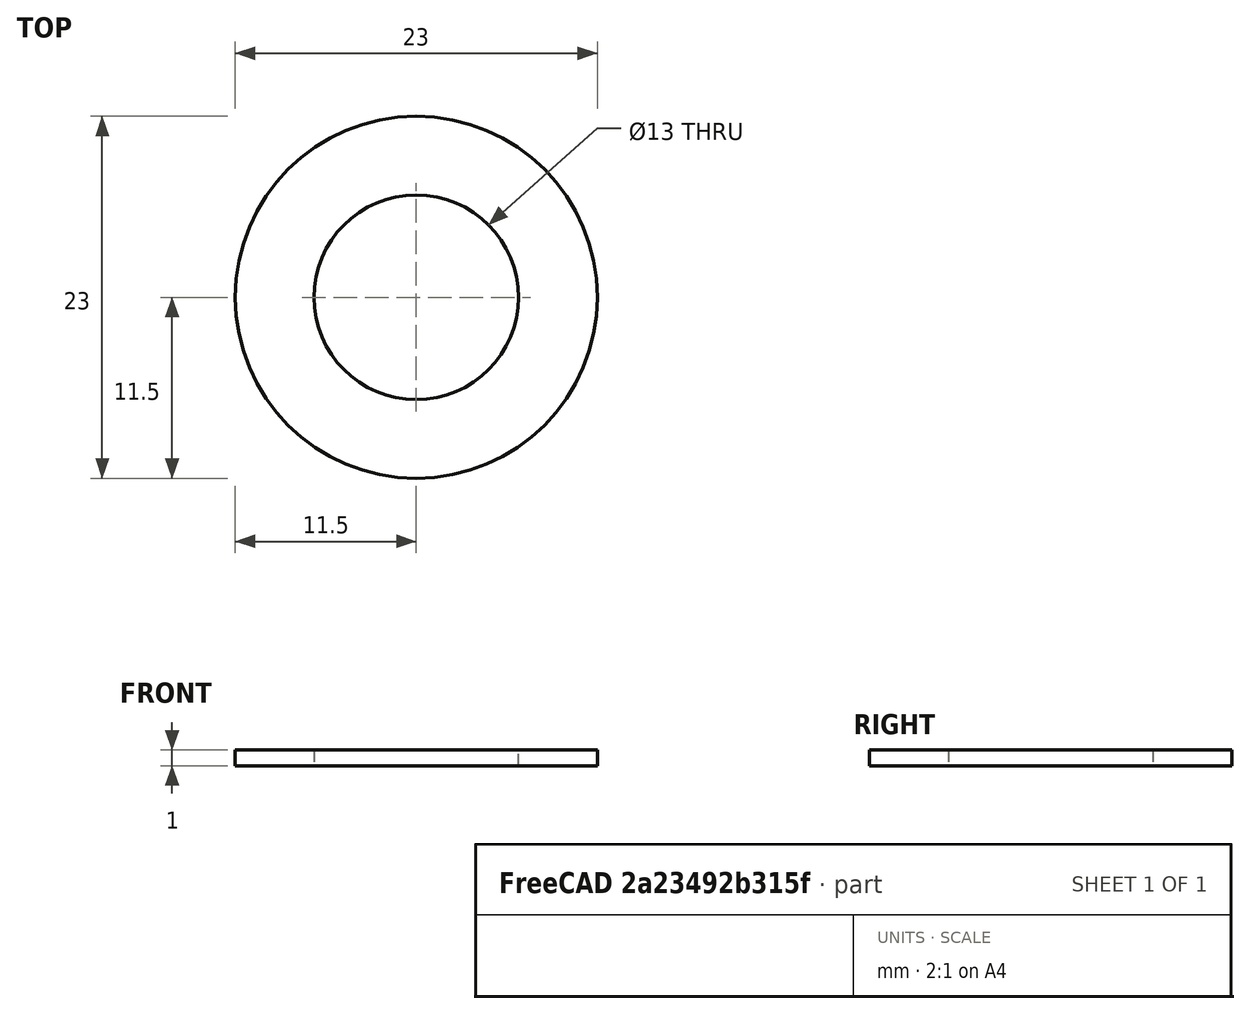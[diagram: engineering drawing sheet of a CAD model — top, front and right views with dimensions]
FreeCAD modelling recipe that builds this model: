
FCSTD DOCUMENT  (FreeCAD 0.19R24276 (Git))
Label: Ring_d13_d23_h1_v2
License: All rights reserved
LicenseURL: http://en.wikipedia.org/wiki/All_rights_reserved
objects: Sketcher::SketchObject×1, PartDesign::Pad×1, PartDesign::Body×1
note: 4 computed .brp shape members not serialized (recipe doc carries the construction recipe); baked Part::Feature solids carry a one-line shape summary decoded from their .brp

FEATURE [Sketcher::SketchObject] Sketch
  FullyConstrained = true
  MapMode = 5
  Support = -> [XY_Plane]
  sketch-geometry (2):
    g0: Circle CenterX=0 CenterY=0 CenterZ=0 NormalX=0 NormalY=0 NormalZ=1 AngleXU=0 Radius=6.5
    g1: Circle CenterX=0 CenterY=0 CenterZ=0 NormalX=0 NormalY=0 NormalZ=1 AngleXU=0 Radius=11.5
  constraints (4):
    c: Coincident(g0,g-1)
    c: Coincident(g1,g0)
    c: Diameter(g0) = 13
    c: Diameter(g1) = 23
FEATURE [PartDesign::Pad] Pad
  Direction = (1,1,1)
  Length = 1
  Length2 = 100
  Profile = -> Sketch
  Type = 0
FEATURE [PartDesign::Body] Body
  Group = -> [Sketch,Pad]
  Origin = -> Origin
  Tip = -> Pad
